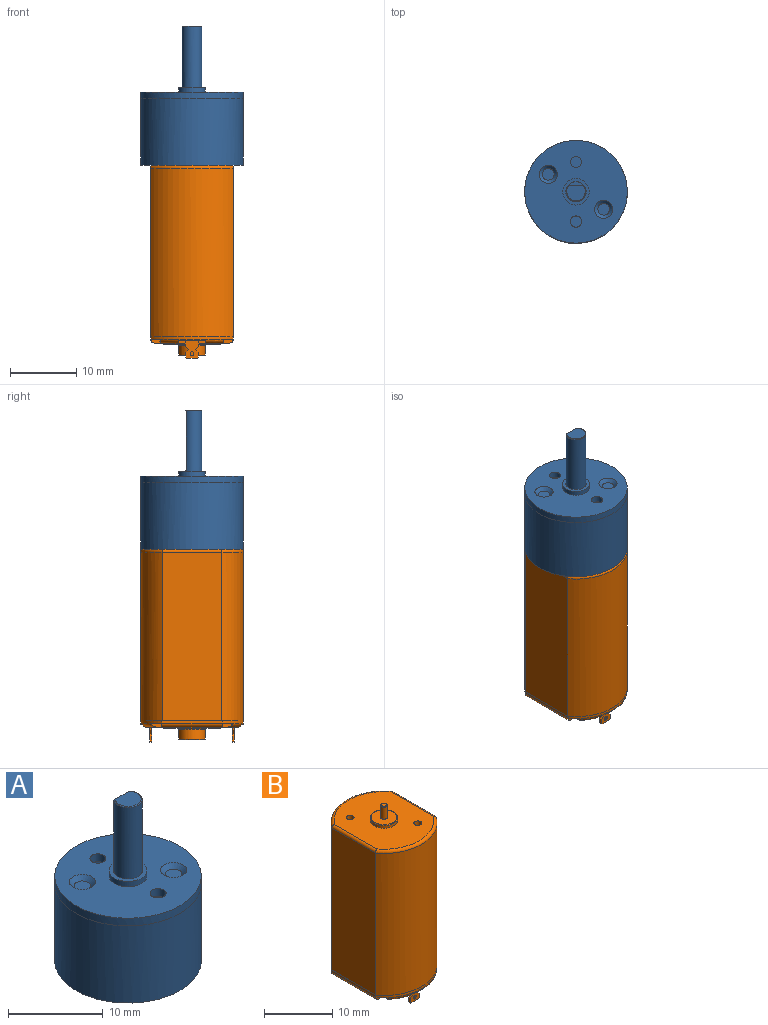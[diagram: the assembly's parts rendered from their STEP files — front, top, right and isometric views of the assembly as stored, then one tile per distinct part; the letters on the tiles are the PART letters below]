
ASSEMBLY  parts=2 mates=1
PART A: 27 faces, bbox 15.5x15.5x21 mm
  f0: cylinder r=0.1mm len=2.4mm, axis (-1,0,0), area 0.4mm2, adj f3,f4,f7
  f1: plane 2.8x2.3mm, normal (0,0,1), area 5.4mm2, adj f2,f4,f5,f6
  f2: revolved ~3x1.5mm, area 0.7mm2, adj f1,f5,f6,f7
  f3: plane 2.23x0.5mm, normal (0,0,1), area 0.8mm2, adj f0,f7
  f4: plane 9.16x2.43mm, normal (0,1,0), area 21.9mm2, adj f0,f1,f5,f6,f7
  f5: revolved ~0.97x0.43mm, area 0.2mm2, adj f1,f2,f4,f7
  f6: revolved ~0.97x0.43mm, area 0.2mm2, adj f1,f2,f4,f7
  f7: cylinder r=1.5mm len=9.9mm, axis (0,0,-1), area 67.9mm2, adj f0,f2,f3,f4,f5,f6,f9
  f8: plane 13.5x13.5mm, normal (0,0,1), area 143.1mm2, adj f10
  f9: plane 3.05x3.05mm, normal (0,0,1), area 0.2mm2, adj f7,f11
  f10: cylinder r=6.75mm len=13.5mm, axis (0,0,1), area 305.4mm2, adj f8,f14
  f11: cylinder r=1.52mm len=3.05mm, axis (0,0,-1), area 6.7mm2, adj f9,f15
  f12: plane 1.75x1.75mm, normal (0,0,1), area 2.4mm2, adj f16
  f13: plane 1.75x1.75mm, normal (0,0,1), area 2.4mm2, adj f17
  f14: plane 13.5x13.5mm, normal (0,0,-1), area 138.6mm2, adj f10,f18,f19
  f15: plane 4x4mm, normal (0,0,1), area 5.3mm2, adj f11,f20
  f16: cone r=0mm half-angle=45deg, axis (0,0,1), area 5mm2, adj f12,f21
  f17: cone r=0mm half-angle=45deg, axis (0,0,1), area 5mm2, adj f13,f21
  f18: cylinder r=0.85mm len=1.7mm, axis (0,0,1), area 5.3mm2, adj f14,f21
  f19: cylinder r=0.85mm len=1.7mm, axis (0,0,1), area 5.3mm2, adj f14,f21
  f20: cylinder r=2mm len=4mm, axis (0,0,-1), area 8.8mm2, adj f15,f21
  f21: plane 15.5x15.5mm, normal (0,0,1), area 159.7mm2, adj f16,f17,f18,f19,f20,f22
  f22: cylinder r=7.75mm len=15.5mm, axis (0,0,-1), area 48.7mm2, adj f21,f23
  f23: cylinder r=7.75mm len=15.5mm, axis (0,0,-1), area 486.9mm2, adj f22,f25
  f24: plane 4x4mm, normal (0,0,-1), area 12.6mm2, adj f26
  f25: plane 15.5x15.5mm, normal (0,0,-1), area 176.1mm2, adj f23,f26
  f26: cylinder r=2mm len=4mm, axis (0,0,-1), area 12.6mm2, adj f24,f25
PART B: 99 faces, bbox 13.8x17x32.2 mm
  f0: plane 2.01x2.01mm, normal (0,0,-1), area 3.2mm2, adj f2
  f1: plane 0.88x0.88mm, normal (0,0,1), area 0.5mm2, adj f3,f4
  f2: cylinder r=1mm len=2.01mm, axis (0,0,-1), area 1.6mm2, adj f0,f5
  f3: revolved ~0.98x0.49mm, area 0.2mm2, adj f1,f4,f6
  f4: revolved ~0.98x0.49mm, area 0.2mm2, adj f1,f3,f6
  f5: plane 3.79x3.79mm, normal (0,0,-1), area 8mm2, adj f2,f7,f8
  f6: cylinder r=0.49mm len=2.15mm, axis (0,0,-1), area 6.6mm2, adj f3,f4,f9
  f7: torus R=1.89mm, axis (0,0,-1), area 1mm2, adj f5,f8,f10
  f8: torus R=1.89mm, axis (0,0,-1), area 1mm2, adj f5,f7,f10
  f9: plane 3.79x3.79mm, normal (0,0,1), area 10.5mm2, adj f6,f15,f16
  f10: cylinder r=1.99mm len=3.99mm, axis (0,0,1), area 18.8mm2, adj f7,f8,f19,f20
  f11: plane 0.3x0.13mm, normal (-0.71,0,-0.71), area 0.1mm2, adj f24,f25,f45,f47
  f12: plane 0.3x0.13mm, normal (0.7,0,-0.72), area 0.1mm2, adj f25,f26,f45,f47
  f13: plane 0.3x0.13mm, normal (-0.71,0,-0.71), area 0.1mm2, adj f33,f34,f50,f52
  f14: plane 0.3x0.13mm, normal (0.7,0,-0.72), area 0.1mm2, adj f34,f35,f50,f52
  f15: torus R=1.89mm, axis (0,0,1), area 1mm2, adj f9,f16,f37
  f16: torus R=1.89mm, axis (0,0,1), area 1mm2, adj f9,f15,f37
  f17: plane 1.14x1.14mm, normal (0,0,1), area 1mm2, adj f38
  f18: plane 1.14x1.14mm, normal (0,0,1), area 1mm2, adj f39
  f19: revolved ~4.19x2.09mm, area 1mm2, adj f10,f20,f40
  f20: revolved ~4.19x2.09mm, area 1mm2, adj f10,f19,f40
  f21: cylinder r=0.3mm len=0.6mm, axis (0,1,0), area 0.6mm2, adj f45,f47
  f22: plane 0.48x0.48mm, normal (-0.71,0,-0.7), area 0.2mm2, adj f23,f45,f46,f47
  f23: plane 0.4x0.4mm, normal (-0.7,0,0.71), area 0.2mm2, adj f22,f24,f45,f47
  f24: plane 0.74x0.3mm, normal (-1,0,0), area 0.2mm2, adj f11,f23,f45,f47
  f25: plane 1.6x0.3mm, normal (0,0,-1), area 0.5mm2, adj f11,f12,f45,f47
  f26: plane 0.74x0.3mm, normal (1,0,0), area 0.2mm2, adj f12,f27,f45,f47
  f27: plane 0.4x0.4mm, normal (0.7,0,0.71), area 0.2mm2, adj f26,f28,f45,f47
  f28: plane 0.48x0.47mm, normal (0.71,0,-0.7), area 0.2mm2, adj f27,f45,f47,f48
  f29: cylinder r=0.3mm len=0.6mm, axis (0,-1,0), area 0.6mm2, adj f50,f52
  f30: plane 0.48x0.47mm, normal (0.71,0,-0.7), area 0.2mm2, adj f36,f49,f50,f52
  f31: plane 0.48x0.48mm, normal (-0.71,0,-0.7), area 0.2mm2, adj f32,f50,f51,f52
  f32: plane 0.4x0.4mm, normal (-0.7,0,0.71), area 0.2mm2, adj f31,f33,f50,f52
  f33: plane 0.74x0.3mm, normal (-1,0,0), area 0.2mm2, adj f13,f32,f50,f52
  f34: plane 1.6x0.3mm, normal (0,0,-1), area 0.5mm2, adj f13,f14,f50,f52
  f35: plane 0.74x0.3mm, normal (1,0,0), area 0.2mm2, adj f14,f36,f50,f52
  f36: plane 0.4x0.4mm, normal (0.7,0,0.71), area 0.2mm2, adj f30,f35,f50,f52
  f37: cylinder r=1.99mm len=3.99mm, axis (0,0,-1), area 5.6mm2, adj f15,f16,f53
  f38: cylinder r=0.57mm len=1.14mm, axis (0,0,1), area 3.6mm2, adj f17,f53
  f39: cylinder r=0.57mm len=1.14mm, axis (0,0,1), area 3.6mm2, adj f18,f53
  f40: plane 8.2x8.2mm, normal (0,0,-1), area 39.1mm2, adj f19,f20,f55,f56
  f41: plane 1.9x1.9mm, normal (0,0,-1), area 2.8mm2, adj f57
  f42: plane 1.9x1.9mm, normal (0,0,-1), area 2.8mm2, adj f58
  f43: plane 1.9x1.9mm, normal (0,0,-1), area 2.8mm2, adj f59
  f44: plane 1.9x1.9mm, normal (0,0,-1), area 2.8mm2, adj f60
  f45: plane 2.65x2mm, normal (0,-1,0), area 4.4mm2, adj f11,f12,f21,f22,f23,f24,f25,f26
  f46: plane 0.9x0.3mm, normal (-1,0,0), area 0.3mm2, adj f22,f45,f47,f64
  f47: plane 2.65x2mm, normal (0,1,0), area 4.4mm2, adj f11,f12,f21,f22,f23,f24,f25,f26
  f48: plane 0.9x0.3mm, normal (1,0,0), area 0.3mm2, adj f28,f45,f47,f64
  f49: plane 0.9x0.3mm, normal (1,0,0), area 0.3mm2, adj f30,f50,f52,f72
  f50: plane 2.65x2mm, normal (0,-1,0), area 4.4mm2, adj f13,f14,f29,f30,f31,f32,f33,f34
  f51: plane 0.9x0.3mm, normal (-1,0,0), area 0.3mm2, adj f31,f50,f52,f72
  f52: plane 2.65x2mm, normal (0,1,0), area 4.4mm2, adj f13,f14,f29,f30,f31,f32,f33,f34
  f53: plane 14.6x11.7mm, normal (0,0,1), area 135.6mm2, adj f37,f38,f39,f54,f68,f70,f75
  f54: cylinder r=0.45mm len=9.03mm, axis (0,-1,0), area 6.3mm2, adj f53,f68,f75,f76
  f55: revolved ~8.6x4.3mm, area 4.2mm2, adj f40,f56,f82
  f56: revolved ~8.6x4.3mm, area 4.2mm2, adj f40,f55,f82
  f57: cylinder r=0.95mm len=1.9mm, axis (0,0,-1), area 1.5mm2, adj f41,f82
  f58: cylinder r=0.95mm len=1.9mm, axis (0,0,-1), area 1.5mm2, adj f42,f82
  f59: cylinder r=0.95mm len=1.9mm, axis (0,0,-1), area 1.5mm2, adj f43,f82
  f60: cylinder r=0.95mm len=1.9mm, axis (0,0,-1), area 1.5mm2, adj f44,f82
  f61: plane 4x0.4mm, normal (0,1,0), area 1.6mm2, adj f63,f64,f65,f82
  f62: plane 4x0.4mm, normal (0,-1,0), area 1.6mm2, adj f71,f72,f73,f82
  f63: plane 2.34x0.44mm, normal (1,0,0), area 0.9mm2, adj f61,f64,f82,f84
  f64: plane 4x2.56mm, normal (0,0,-1), area 9.3mm2, adj f45,f46,f47,f48,f61,f63,f65,f84
  f65: plane 2.34x0.44mm, normal (-1,0,0), area 0.9mm2, adj f61,f64,f82,f84
  f66: plane 1.5x0.6mm, normal (0,1,0), area 0.8mm2, adj f67,f77,f82,f85
  f67: plane 1.76x0.81mm, normal (1,0,0), area 0.8mm2, adj f66,f82,f84,f85
  f68: torus R=7.3mm, axis (0,0,1), area 10.1mm2, adj f53,f54,f70,f86
  f69: plane 1.76x0.81mm, normal (-1,0,0), area 0.8mm2, adj f82,f83,f84,f87
  f70: cylinder r=0.45mm len=9.03mm, axis (0,1,0), area 6.3mm2, adj f53,f68,f75,f88
  f71: plane 2.34x0.44mm, normal (-1,0,0), area 0.9mm2, adj f62,f72,f82,f89
  f72: plane 4x2.56mm, normal (0,0,-1), area 9.3mm2, adj f49,f50,f51,f52,f62,f71,f73,f89
  f73: plane 2.34x0.44mm, normal (1,0,0), area 0.9mm2, adj f62,f72,f82,f89
  f74: plane 1.76x0.81mm, normal (-1,0,0), area 0.8mm2, adj f81,f82,f89,f90
  f75: torus R=7.3mm, axis (0,0,1), area 10.1mm2, adj f53,f54,f70,f91
  f76: plane 25.45x9.03mm, normal (1,0,0), area 229.7mm2, adj f54,f78,f86,f91
  f77: cylinder r=0.6mm len=9.14mm, axis (0,1,0), area 8.6mm2, adj f66,f80,f82,f92
  f78: plane 9.14x0.04mm, normal (0,0,-1), area 0.4mm2, adj f76,f86,f91,f92
  f79: plane 1.76x0.81mm, normal (1,0,0), area 0.8mm2, adj f80,f82,f89,f93
  f80: plane 1.5x0.6mm, normal (0,-1,0), area 0.8mm2, adj f77,f79,f82,f93
  f81: plane 1.5x0.6mm, normal (0,-1,0), area 0.8mm2, adj f74,f82,f90,f94
  f82: plane 13.82x11.41mm, normal (0,0,-1), area 57.1mm2, adj f55,f56,f57,f58,f59,f60,f61,f62
  f83: plane 1.5x0.6mm, normal (0,1,0), area 0.8mm2, adj f69,f82,f87,f94
  f84: revolved ~10.32x2.42mm, area 6.9mm2, adj f63,f64,f65,f67,f69,f82,f95
  f85: plane 1.55x1.5mm, normal (0,0,-1), area 1.3mm2, adj f66,f67,f95
  f86: cylinder r=7.75mm len=25.45mm, axis (0,0,-1), area 374.4mm2, adj f68,f76,f78,f88,f95,f96
  f87: plane 1.55x1.5mm, normal (0,0,-1), area 1.3mm2, adj f69,f83,f95
  f88: plane 25.45x9.03mm, normal (-1,0,0), area 229.7mm2, adj f70,f86,f91,f96
  f89: revolved ~10.32x2.42mm, area 6.9mm2, adj f71,f72,f73,f74,f79,f82,f97
  f90: plane 1.55x1.5mm, normal (0,0,-1), area 1.3mm2, adj f74,f81,f97
  f91: cylinder r=7.75mm len=25.45mm, axis (0,0,-1), area 374.4mm2, adj f75,f76,f78,f88,f96,f97
  f92: plane 9.14x0.4mm, normal (1,0,0), area 3.7mm2, adj f77,f78,f95,f97
  f93: plane 1.55x1.5mm, normal (0,0,-1), area 1.3mm2, adj f79,f80,f97
  f94: cylinder r=0.6mm len=9.14mm, axis (0,-1,0), area 8.6mm2, adj f81,f82,f83,f98
  f95: cylinder r=7.75mm len=12.52mm, axis (0,0,1), area 5.8mm2, adj f84,f85,f86,f87,f92,f98
  f96: plane 9.14x0.04mm, normal (0,0,-1), area 0.4mm2, adj f86,f88,f91,f98
  f97: cylinder r=7.75mm len=12.52mm, axis (0,0,1), area 5.8mm2, adj f89,f90,f91,f92,f93,f98
  f98: plane 9.14x0.4mm, normal (-1,0,0), area 3.7mm2, adj f94,f95,f96,f97
PLACE A t=(-0.04,-0.3,10.24)mm
PLACE B t=(-0.04,-0.3,-15.66)mm
MATE fastened A.f7 <-> B.f2  axis (0,0,-1) through (-0.04,-0.3,10.24)mm
